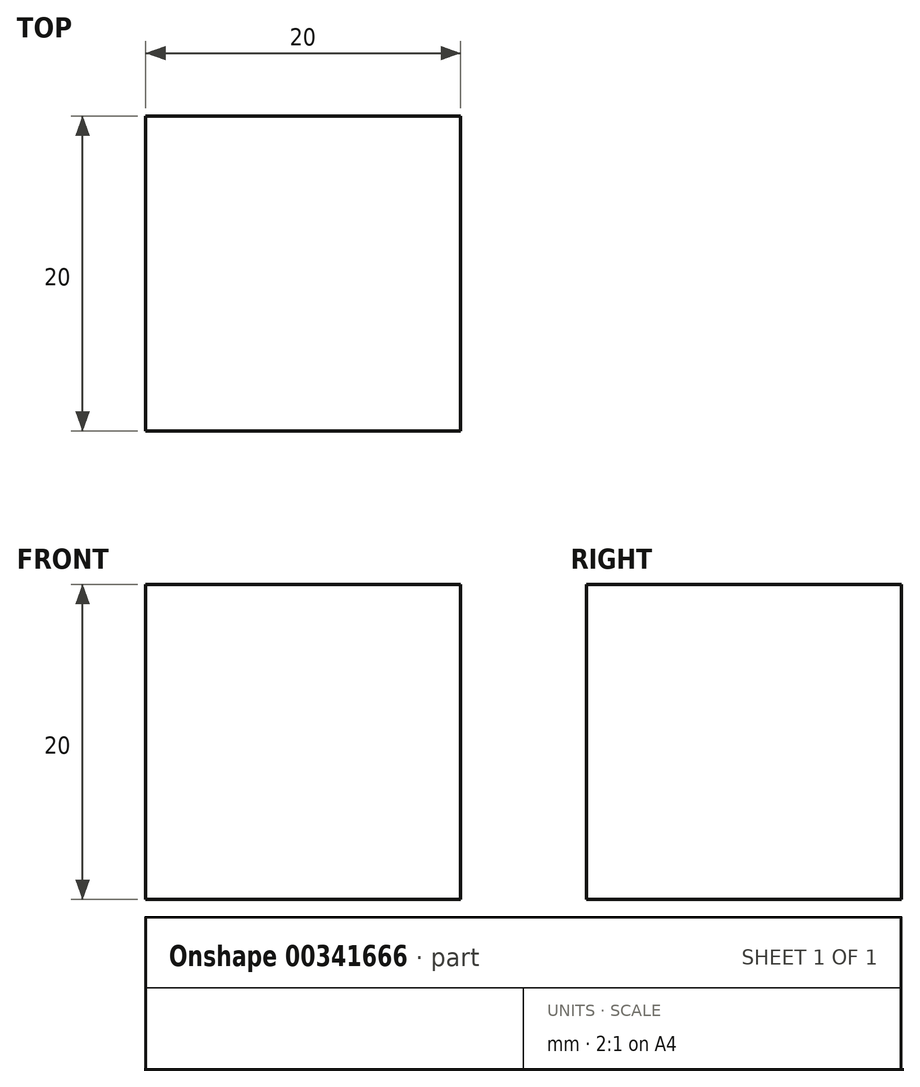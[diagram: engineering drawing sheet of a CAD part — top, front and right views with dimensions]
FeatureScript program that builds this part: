
annotation { "Feature Type Name" : "Feature", "Feature Type Description" : "" }
export const myFeature = defineFeature(function(context is Context, id is Id, definition is map)
    precondition{}
    {
        {
            var Q0;
            Q0=qCreatedBy(makeId("Top.planeOp"),FACE);
            var sketch = newSketch(context, id + "F0", { "sketchPlane" : qUnion([Q0])});
            skLineSegment(sketch, "E0.bottom", {"start": v(-10, 10) * mm, "end": v(10, 10) * mm});
            skLineSegment(sketch, "E0.top", {"start": v(-10, -10) * mm, "end": v(10, -10) * mm});
            skLineSegment(sketch, "E0.left", {"start": v(-10, 10) * mm, "end": v(-10, -10) * mm});
            skLineSegment(sketch, "E0.right", {"start": v(10, 10) * mm, "end": v(10, -10) * mm});
            skPoint(sketch, "E0.middle", {"position": v(0, 0) * mm});
            skSolve(sketch);
        }
        {
            var Q0;
            Q0=makeQuery(id+"F0.imprint","IMPRINT",FACE,{"disambiguationData":[TD([[makeQuery(id+"F0.imprint","IMPRINT",EDGE,{"derivedFrom":sQuery(id+"F0.wireOp",EDGE,"E0.bottom")}),-1.0]])]});
            extrude(context, id + "F1", {"entities" : qUnion([Q0]), "depth" : 20 * mm});
        }
    });
